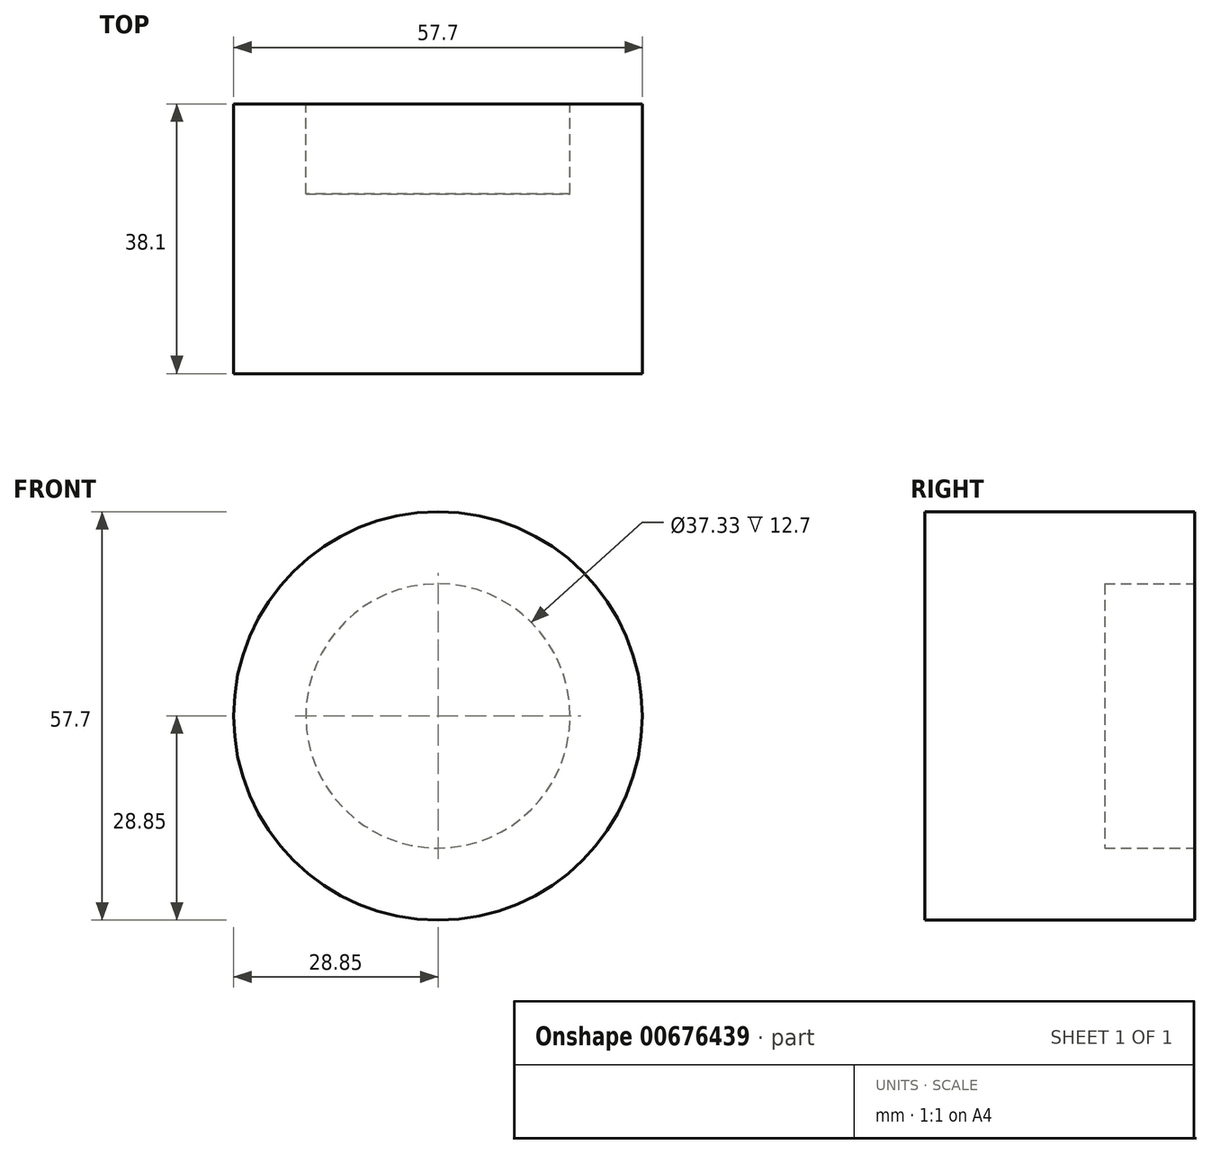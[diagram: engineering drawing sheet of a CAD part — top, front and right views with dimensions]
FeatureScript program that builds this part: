
annotation { "Feature Type Name" : "Feature", "Feature Type Description" : "" }
export const myFeature = defineFeature(function(context is Context, id is Id, definition is map)
    precondition{}
    {
        {
            var Q0;
            Q0=qCreatedBy(makeId("Front.planeOp"),FACE);
            var sketch = newSketch(context, id + "F0", { "sketchPlane" : qUnion([Q0])});
            skCircle(sketch, "E0", {"center": v(0, 0) * mm, "radius": 18.64 * mm});
            skSolve(sketch);
        }
        {
            var Q0;
            Q0=makeQuery(id+"F0.imprint","IMPRINT",FACE,{"disambiguationData":[TD([[makeQuery(id+"F0.imprint","IMPRINT",EDGE,{"derivedFrom":sQuery(id+"F0.wireOp",EDGE,"E0")}),1.0]])]});
            extrude(context, id + "F1", {"entities" : qUnion([Q0]), "depth" : 11.43 * mm, "offsetDistance" : 25.4 * mm});
        }
        {
            var Q0;
            Q0=qCreatedBy(makeId("Front.planeOp"),FACE);
            var sketch = newSketch(context, id + "F2", { "sketchPlane" : qUnion([Q0])});
            skCircle(sketch, "E1", {"center": v(0, 0) * mm, "radius": 28.85 * mm});
            skSolve(sketch);
        }
        {
            var Q0;
            Q0 = qSketchRegion(id + "F2", true);
            extrude(context, id + "F3", {"entities" : qUnion([Q0]), "operationType" : NewBodyOperationType.ADD, "depth" : 38.1 * mm, "offsetDistance" : 25.4 * mm});
        }
        {
            var Q0;
            Q0=makeQuery(id+"F3.boolean.opBoolean","MERGE",FACE,{"derivedFrom":[makeQuery(id+"F1.opExtrude","CAP_FACE",FACE,{"disambiguationData":[OSD([sQuery(id+"F0.wireOp",EDGE,"E0")])],"isStart":true}),makeQuery(id+"F3.opExtrude","CAP_FACE",FACE,{"disambiguationData":[OSD([sQuery(id+"F2.wireOp",EDGE,"E1")])],"isStart":true})]});
            var sketch = newSketch(context, id + "F4", { "sketchPlane" : qUnion([Q0])});
            skCircle(sketch, "E2", {"center": v(0, 0) * mm, "radius": 18.66 * mm});
            skSolve(sketch);
        }
        {
            var Q0;
            Q0=makeQuery(id+"F4.imprint","IMPRINT",FACE,{"disambiguationData":[TD([[makeQuery(id+"F4.imprint","IMPRINT",EDGE,{"derivedFrom":sQuery(id+"F4.wireOp",EDGE,"E2")}),1.0]])]});
            var Q1;
            Q1=makeQuery(id+"F3.opExtrude","CAP_FACE",FACE,{"disambiguationData":[OSD([sQuery(id+"F2.wireOp",EDGE,"E1")])],"isStart":false});
            extrude(context, id + "F5", {"entities" : qUnion([Q0, Q1]), "operationType" : NewBodyOperationType.REMOVE, "oppositeDirection" : true, "depth" : 12.7 * mm, "offsetDistance" : 25.4 * mm});
        }
    });
